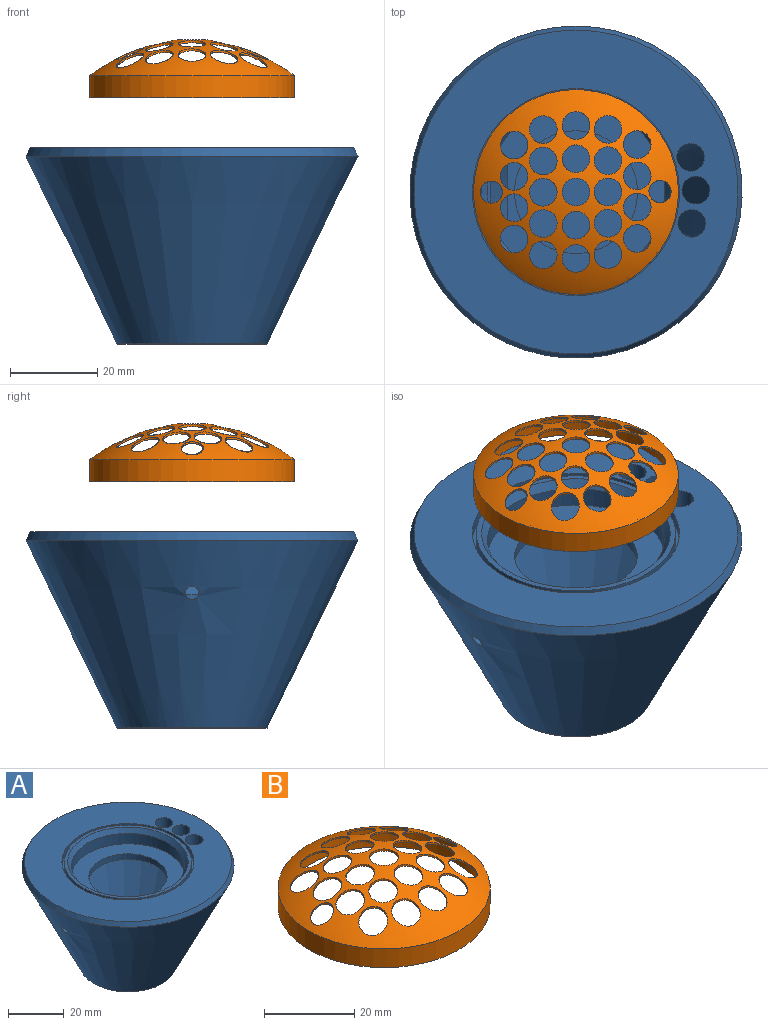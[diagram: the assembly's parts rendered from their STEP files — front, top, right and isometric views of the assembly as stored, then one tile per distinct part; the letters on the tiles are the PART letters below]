
ASSEMBLY  parts=2 mates=1
PART A: 28 faces, bbox 76.2x76.2x45.1 mm
  f0: plane 45.72x45.72mm, normal (0,0,1), area 169.4mm2, adj f9,f25
  f1: cone r=31.87mm half-angle=25.8deg, axis (0,0,1), area 5532.9mm2, adj f4,f5,f20,f21
  f2: cone r=38.1mm half-angle=25.8deg, axis (0,0,1), area 8319.1mm2, adj f11,f12,f20
  f3: plane 30.61x30.61mm, normal (0,0,1), area 736mm2, adj f4
  f4: torus R=15.31mm, axis (0,0,-1), area 55.7mm2, adj f1,f3
  f5: plane 63.75x63.75mm, normal (0,0,-1), area 2420.8mm2, adj f1,f6,f14,f15,f16,f17,f18,f19
  f6: cylinder r=14.09mm len=28.19mm, axis (0,0,-1), area 218.4mm2, adj f5,f7
  f7: plane 40.64x40.64mm, normal (0,0,1), area 621.1mm2, adj f6,f8,f14,f15,f16,f17,f18,f19
  f8: cylinder r=20.32mm len=40.64mm, axis (0,0,-1), area 583.7mm2, adj f7,f9
  f9: cone r=21.65mm half-angle=35.5deg, axis (0,0,1), area 301.8mm2, adj f0,f8
  f10: plane 74.35x74.35mm, normal (0,0,1), area 2475mm2, adj f11,f22,f23,f24,f26
  f11: cone r=38.1mm half-angle=26.4deg, axis (0,0,-1), area 492mm2, adj f2,f10
  f12: torus R=16.79mm, axis (0,0,-1), area 8.7mm2, adj f2,f13
  f13: plane 34.42x34.42mm, normal (0,0,-1), area 930.6mm2, adj f12
  f14: plane 5.72x2.47mm, normal (1,0,0), area 14.1mm2, adj f5,f7,f15,f19
  f15: cylinder r=5.08mm len=4.76mm, axis (0,0,1), area 15.2mm2, adj f5,f7,f14,f16
  f16: cylinder r=0.51mm len=2.47mm, axis (0,0,1), area 2.4mm2, adj f5,f7,f15,f17
  f17: plane 14.28x2.47mm, normal (-1,0,0), area 35.2mm2, adj f5,f7,f16,f18
  f18: cylinder r=0.51mm len=2.47mm, axis (0,0,1), area 2.4mm2, adj f5,f7,f17,f19
  f19: cylinder r=5.08mm len=4.76mm, axis (0,0,1), area 15.2mm2, adj f5,f7,f14,f18
  f20: cylinder r=1.52mm len=3.77mm, axis (1,0,0), area 25.7mm2, adj f1,f2,f21
  f21: plane 2.98x1.17mm, normal (-1,0,0), area 2.4mm2, adj f1,f20
  f22: cylinder r=3.17mm len=8.9mm, axis (0,0,1), area 177.6mm2, adj f5,f10
  f23: cylinder r=3.17mm len=8.9mm, axis (0,0,1), area 177.6mm2, adj f5,f10
  f24: cylinder r=3.17mm len=8.9mm, axis (0,0,1), area 177.6mm2, adj f5,f10
  f25: cylinder r=22.86mm len=45.72mm, axis (0,0,1), area 364.8mm2, adj f0,f27
  f26: cylinder r=23.75mm len=47.5mm, axis (0,0,1), area 379mm2, adj f10,f27
  f27: plane 47.5x47.5mm, normal (0,0,1), area 130.2mm2, adj f25,f26
PART B: 30 faces, bbox 47x47x13.3 mm
  f0: cylinder r=23.49mm len=46.99mm, axis (0,0,1), area 749.9mm2, adj f1,f4
  f1: revolved ~46.99x46.99mm, area 3956.8mm2, adj f0,f5,f6,f7,f8,f9,f10,f11
  f2: revolved ~45.97x45.97mm, area 2974.1mm2, adj f3,f5,f6,f7,f8,f9,f10,f11
  f3: cylinder r=22.99mm len=45.97mm, axis (0,0,1), area 733.7mm2, adj f2,f4
  f4: plane 46.99x46.99mm, normal (0,0,-1), area 74.2mm2, adj f0,f3
  f5: cylinder r=3.17mm len=6.35mm, axis (0,0,1), area 8.4mm2, adj f1,f2
  f6: cylinder r=3.17mm len=6.35mm, axis (0,0,1), area 9.5mm2, adj f1,f2
  f7: cylinder r=3.17mm len=6.35mm, axis (0,0,1), area 8.5mm2, adj f1,f2
  f8: cylinder r=3.17mm len=6.35mm, axis (0,0,1), area 8.3mm2, adj f1,f2
  f9: cylinder r=3.17mm len=6.35mm, axis (0,0,1), area 8.8mm2, adj f1,f2
  f10: cylinder r=2.54mm len=5.08mm, axis (0,0,1), area 6.4mm2, adj f1,f2
  f11: cylinder r=2.54mm len=5.08mm, axis (0,0,1), area 6.4mm2, adj f1,f2
  f12: cylinder r=3.17mm len=6.35mm, axis (0,0,1), area 8.3mm2, adj f1,f2
  f13: cylinder r=3.17mm len=6.35mm, axis (0,0,1), area 8.7mm2, adj f1,f2
  f14: cylinder r=3.17mm len=6.35mm, axis (0,0,1), area 8.7mm2, adj f1,f2
  f15: cylinder r=3.17mm len=6.35mm, axis (0,0,1), area 10mm2, adj f1,f2
  f16: cylinder r=3.17mm len=6.35mm, axis (0,0,1), area 11mm2, adj f1,f2
  f17: cylinder r=3.17mm len=6.35mm, axis (0,0,1), area 10mm2, adj f1,f2
  f18: cylinder r=3.17mm len=6.35mm, axis (0,0,1), area 8.6mm2, adj f1,f2
  f19: cylinder r=3.17mm len=6.35mm, axis (0,0,1), area 8.5mm2, adj f1,f2
  f20: cylinder r=3.17mm len=6.35mm, axis (0,0,1), area 9.5mm2, adj f1,f2
  f21: cylinder r=3.17mm len=6.35mm, axis (0,0,1), area 10mm2, adj f1,f2
  f22: cylinder r=3.17mm len=6.35mm, axis (0,0,1), area 8.8mm2, adj f1,f2
  f23: cylinder r=3.17mm len=6.35mm, axis (0,0,1), area 8.8mm2, adj f1,f2
  f24: cylinder r=3.17mm len=6.35mm, axis (0,0,1), area 8.3mm2, adj f1,f2
  f25: cylinder r=3.17mm len=6.35mm, axis (0,0,1), area 8.5mm2, adj f1,f2
  f26: cylinder r=3.17mm len=6.35mm, axis (0,0,1), area 9.5mm2, adj f1,f2
  f27: cylinder r=3.17mm len=6.35mm, axis (0,0,1), area 10mm2, adj f1,f2
  f28: cylinder r=3.17mm len=6.35mm, axis (0,0,1), area 9.5mm2, adj f1,f2
  f29: cylinder r=3.17mm len=6.35mm, axis (0,0,1), area 8.5mm2, adj f1,f2
PLACE A t=(-2.83,0.52,-29.19)mm
PLACE B t=(-2.83,7.67,36.91)mm
MATE slider B.f0 <-> A.f9  axis (0,0,1) through (-2.83,7.67,41.99)mm
